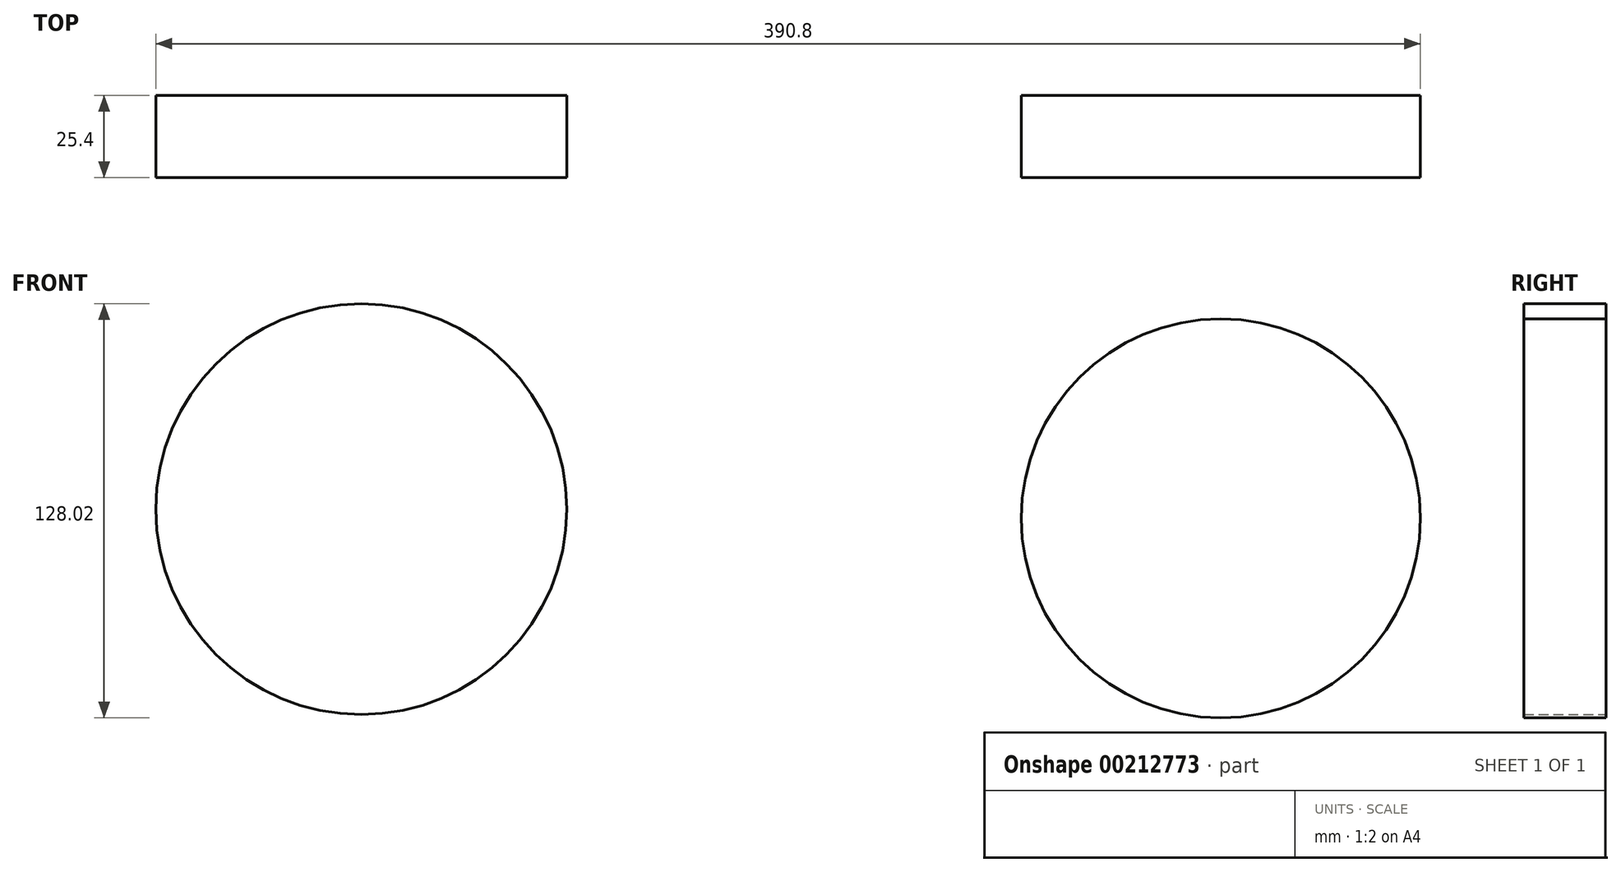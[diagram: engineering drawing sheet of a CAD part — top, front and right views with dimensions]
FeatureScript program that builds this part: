
annotation { "Feature Type Name" : "Feature", "Feature Type Description" : "" }
export const myFeature = defineFeature(function(context is Context, id is Id, definition is map)
    precondition{}
    {
        {
            var Q0;
            Q0=qCreatedBy(makeId("Front.planeOp"),FACE);
            var sketch = newSketch(context, id + "F0", { "sketchPlane" : qUnion([Q0])});
            skCircle(sketch, "E0", {"center": v(-182.7, 39.69) * mm, "radius": 63.5 * mm});
            skCircle(sketch, "E1", {"center": v(82.92, 36.85) * mm, "radius": 61.68 * mm});
            skLineSegment(sketch, "E2", {"start": v(-119.3, 36.2) * mm, "end": v(21.25, 36.2) * mm});
            skLineSegment(sketch, "E3.0", {"start": v(-119.3, 61.6) * mm, "end": v(21.25, 61.6) * mm});
            skSolve(sketch);
        }
        {
            var Q0;
            Q0=makeQuery(id+"F0.imprint","IMPRINT",FACE,{"disambiguationData":[TD([[makeQuery(id+"F0.imprint","IMPRINT",EDGE,{"derivedFrom":sQuery(id+"F0.wireOp",EDGE,"E0")}),1.0]])]});
            var Q1;
            Q1=makeQuery(id+"F0.imprint","IMPRINT",FACE,{"disambiguationData":[TD([[makeQuery(id+"F0.imprint","IMPRINT",EDGE,{"derivedFrom":sQuery(id+"F0.wireOp",EDGE,"E1")}),1.0]])]});
            extrude(context, id + "F1", {"entities" : qUnion([Q0, Q1]), "depth" : 25.4 * mm});
        }
    });
